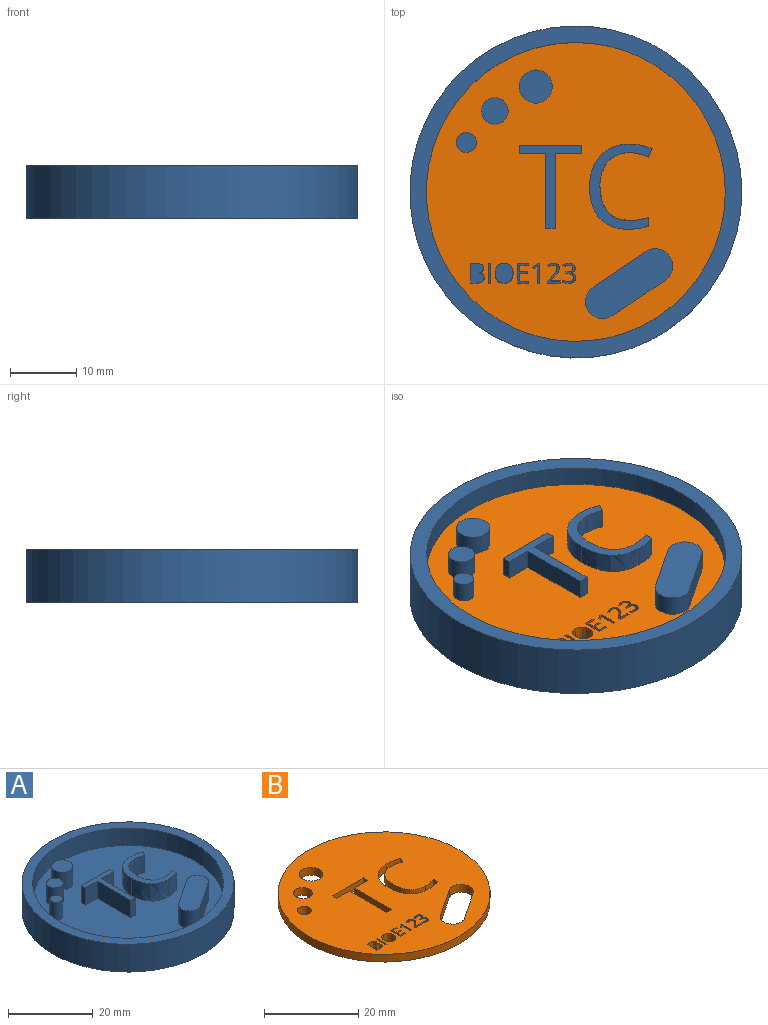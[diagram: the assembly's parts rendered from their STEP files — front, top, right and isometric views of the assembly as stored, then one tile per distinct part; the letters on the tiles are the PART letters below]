
ASSEMBLY  parts=2 mates=1
PART A: 41 faces, bbox 50x50x8 mm
  f0: cylinder r=22.5mm len=45mm, axis (0,0,-1), area 706.9mm2, adj f2,f40
  f1: cylinder r=25mm len=50mm, axis (0,0,-1), area 1256.6mm2, adj f2,f3
  f2: plane 50x50mm, normal (0,0,1), area 373.1mm2, adj f0,f1
  f3: plane 50x50mm, normal (0,0,-1), area 1963.5mm2, adj f1
  f4: cylinder r=1.5mm len=5mm, axis (0,0,-1), area 47.1mm2, adj f5,f40
  f5: plane 3x3mm, normal (0,0,1), area 7.1mm2, adj f4
  f6: cylinder r=2mm len=5mm, axis (0,0,-1), area 62.8mm2, adj f7,f40
  f7: plane 4x4mm, normal (0,0,1), area 12.6mm2, adj f6
  f8: cylinder r=2.5mm len=5mm, axis (0,0,-1), area 78.5mm2, adj f9,f40
  f9: plane 5x5mm, normal (0,0,1), area 19.6mm2, adj f8
  f10: plane 11.18x5mm, normal (1,0,0), area 55.9mm2, adj f11,f17,f18,f40
  f11: plane 5x3.95mm, normal (0,-1,0), area 19.7mm2, adj f10,f12,f18,f40
  f12: plane 5x1.29mm, normal (1,0,0), area 6.4mm2, adj f11,f13,f18,f40
  f13: plane 9.34x5mm, normal (0,1,0), area 46.7mm2, adj f12,f14,f18,f40
  f14: plane 5x1.29mm, normal (-1,0,0), area 6.4mm2, adj f13,f15,f18,f40
  f15: plane 5x3.95mm, normal (0,-1,0), area 19.7mm2, adj f14,f16,f18,f40
  f16: plane 11.18x5mm, normal (-1,0,0), area 55.9mm2, adj f15,f17,f18,f40
  f17: plane 5x1.45mm, normal (0,-1,0), area 7.2mm2, adj f10,f16,f18,f40
  f18: plane 12.47x9.34mm, normal (0,0,1), area 28.2mm2, adj f10,f11,f12,f13,f14,f15,f16,f17
  f19: extruded ~5x2.83mm, area 14.7mm2, adj f20,f33,f34,f40
  f20: plane 5x1.24mm, normal (0.9,-0.44,0), area 6.9mm2, adj f19,f21,f34,f40
  f21: extruded ~5x3.43mm, area 17.7mm2, adj f20,f22,f34,f40
  f22: extruded ~5x3.2mm, area 16.7mm2, adj f21,f23,f34,f40
  f23: extruded ~5x2.23mm, area 15.5mm2, adj f22,f24,f34,f40
  f24: extruded ~5x3.37mm, area 17.4mm2, adj f23,f25,f34,f40
  f25: extruded ~5x4.75mm, area 25.5mm2, adj f24,f26,f34,f40
  f26: extruded ~5x4.25mm, area 23.6mm2, adj f25,f27,f34,f40
  f27: extruded ~5x3.2mm, area 16.3mm2, adj f26,f28,f34,f40
  f28: plane 5x1.27mm, normal (1,0,0), area 6.3mm2, adj f27,f29,f34,f40
  f29: extruded ~5x2.98mm, area 15.1mm2, adj f28,f30,f34,f40
  f30: extruded ~5x3.27mm, area 18.3mm2, adj f29,f31,f34,f40
  f31: extruded ~5x3.78mm, area 20.2mm2, adj f30,f32,f34,f40
  f32: extruded ~5x3.75mm, area 20.1mm2, adj f31,f33,f34,f40
  f33: extruded ~5x3.24mm, area 18.2mm2, adj f19,f32,f34,f40
  f34: plane 12.81x9.43mm, normal (0,0,1), area 34mm2, adj f19,f20,f21,f22,f23,f24,f25,f26
  f35: plane 7.94x5.33mm, normal (-0.56,0.83,0), area 47.8mm2, adj f36,f38,f39,f40
  f36: cylinder r=2.61mm len=5mm, axis (0,0,-1), area 41mm2, adj f35,f37,f39,f40
  f37: plane 7.94x5.33mm, normal (0.56,-0.83,0), area 47.8mm2, adj f36,f38,f39,f40
  f38: cylinder r=2.61mm len=5mm, axis (0,0,-1), area 41mm2, adj f35,f37,f39,f40
  f39: plane 13.15x10.55mm, normal (0,0,1), area 71.2mm2, adj f35,f36,f37,f38
  f40: plane 45x45mm, normal (0,0,1), area 1417.7mm2, adj f0,f4,f6,f8,f10,f11,f12,f13
PART B: 125 faces, bbox 45x45x2 mm
  f0: plane 7.94x5.33mm, normal (0.56,-0.83,0), area 19.1mm2, adj f1,f109,f123,f124
  f1: cylinder r=2.61mm len=4.77mm, axis (0,0,-1), area 16.4mm2, adj f0,f2,f123,f124
  f2: plane 7.94x5.33mm, normal (-0.56,0.83,0), area 19.1mm2, adj f1,f109,f123,f124
  f3: plane 3.95x2mm, normal (0,1,0), area 7.9mm2, adj f4,f110,f123,f124
  f4: plane 11.18x2mm, normal (-1,0,0), area 22.4mm2, adj f3,f5,f123,f124
  f5: plane 2x1.45mm, normal (0,1,0), area 2.9mm2, adj f4,f6,f123,f124
  f6: plane 11.18x2mm, normal (1,0,0), area 22.4mm2, adj f5,f7,f123,f124
  f7: plane 3.95x2mm, normal (0,1,0), area 7.9mm2, adj f6,f8,f123,f124
  f8: plane 2x1.29mm, normal (1,0,0), area 2.6mm2, adj f7,f9,f123,f124
  f9: plane 9.34x2mm, normal (0,-1,0), area 18.7mm2, adj f8,f110,f123,f124
  f10: plane 2x1.24mm, normal (-0.9,0.44,0), area 2.8mm2, adj f11,f111,f123,f124
  f11: extruded ~2.83x2mm, area 5.9mm2, adj f10,f12,f123,f124
  f12: extruded ~3.24x2mm, area 7.3mm2, adj f11,f13,f123,f124
  f13: extruded ~3.75x2mm, area 8mm2, adj f12,f14,f123,f124
  f14: extruded ~3.78x2mm, area 8.1mm2, adj f13,f15,f123,f124
  f15: extruded ~3.27x2mm, area 7.3mm2, adj f14,f16,f123,f124
  f16: extruded ~2.98x2mm, area 6mm2, adj f15,f17,f123,f124
  f17: plane 2x1.27mm, normal (-1,0,0), area 2.5mm2, adj f16,f18,f123,f124
  f18: extruded ~3.2x2mm, area 6.5mm2, adj f17,f19,f123,f124
  f19: extruded ~4.25x2mm, area 9.4mm2, adj f18,f20,f123,f124
  f20: extruded ~4.75x2mm, area 10.2mm2, adj f19,f21,f123,f124
  f21: extruded ~3.37x2mm, area 7mm2, adj f20,f22,f123,f124
  f22: extruded ~2.23x2.08mm, area 6.2mm2, adj f21,f23,f123,f124
  f23: extruded ~3.2x2mm, area 6.7mm2, adj f22,f111,f123,f124
  f24: plane 2x1.03mm, normal (0,1,0), area 2.1mm2, adj f25,f112,f123,f124
  f25: plane 2.96x2mm, normal (1,0,0), area 5.9mm2, adj f24,f26,f123,f124
  f26: plane 2x0.84mm, normal (0,-1,0), area 1.7mm2, adj f25,f27,f123,f124
  f27: extruded ~2x0.85mm, area 1.8mm2, adj f26,f28,f123,f124
  f28: extruded ~2x0.56mm, area 1.3mm2, adj f27,f29,f123,f124
  f29: extruded ~2x0.43mm, area 0.9mm2, adj f28,f30,f123,f124
  f30: extruded ~2x0.43mm, area 1mm2, adj f29,f31,f123,f124
  f31: plane 2x0.02mm, normal (-1,0,0), area 0mm2, adj f30,f32,f123,f124
  f32: extruded ~2x0.71mm, area 2.2mm2, adj f31,f33,f123,f124
  f33: extruded ~2x0.62mm, area 1.4mm2, adj f32,f112,f123,f124
  f34: plane 2.96x2mm, normal (-1,0,0), area 5.9mm2, adj f35,f113,f123,f124
  f35: plane 2x0.34mm, normal (0,1,0), area 0.7mm2, adj f34,f36,f123,f124
  f36: plane 2.96x2mm, normal (1,0,0), area 5.9mm2, adj f35,f113,f123,f124
  f37: extruded ~2x1mm, area 2.2mm2, adj f38,f114,f123,f124
  f38: extruded ~2x1.12mm, area 2.4mm2, adj f37,f39,f123,f124
  f39: extruded ~2x1.12mm, area 2.4mm2, adj f38,f40,f123,f124
  f40: extruded ~2x1mm, area 2.2mm2, adj f39,f41,f123,f124
  f41: extruded ~2x1.01mm, area 2.2mm2, adj f40,f42,f123,f124
  f42: extruded ~2x1.13mm, area 2.4mm2, adj f41,f43,f123,f124
  f43: extruded ~2x1.12mm, area 2.4mm2, adj f42,f114,f123,f124
  f44: plane 2x1.31mm, normal (0,-1,0), area 2.6mm2, adj f45,f115,f123,f124
  f45: plane 2x0.31mm, normal (-1,0,0), area 0.6mm2, adj f44,f46,f123,f124
  f46: plane 2x1.65mm, normal (0,1,0), area 3.3mm2, adj f45,f47,f123,f124
  f47: plane 2.96x2mm, normal (1,0,0), area 5.9mm2, adj f46,f48,f123,f124
  f48: plane 2x1.65mm, normal (0,-1,0), area 3.3mm2, adj f47,f49,f123,f124
  f49: plane 2x0.31mm, normal (-1,0,0), area 0.6mm2, adj f48,f50,f123,f124
  f50: plane 2x1.31mm, normal (0,1,0), area 2.6mm2, adj f49,f51,f123,f124
  f51: plane 2x0.95mm, normal (-1,0,0), area 1.9mm2, adj f50,f52,f123,f124
  f52: plane 2x1.23mm, normal (0,-1,0), area 2.5mm2, adj f51,f53,f123,f124
  f53: plane 2x0.3mm, normal (-1,0,0), area 0.6mm2, adj f52,f54,f123,f124
  f54: plane 2x1.23mm, normal (0,1,0), area 2.5mm2, adj f53,f115,f123,f124
  f55: plane 2x0.28mm, normal (0,-1,0), area 0.6mm2, adj f56,f116,f123,f124
  f56: plane 2.96x2mm, normal (-1,0,0), area 5.9mm2, adj f55,f57,f123,f124
  f57: plane 2x0.33mm, normal (0,1,0), area 0.7mm2, adj f56,f58,f123,f124
  f58: plane 2.11x2mm, normal (1,0,0), area 4.2mm2, adj f57,f59,f123,f124
  f59: extruded ~2x0.5mm, area 1mm2, adj f58,f60,f123,f124
  f60: extruded ~2x0.1mm, area 0.3mm2, adj f59,f61,f123,f124
  f61: extruded ~2x0.48mm, area 1.2mm2, adj f60,f62,f123,f124
  f62: plane 2x0.23mm, normal (0.79,0.61,0), area 0.6mm2, adj f61,f116,f123,f124
  f63: plane 2x1.52mm, normal (0,-1,0), area 3mm2, adj f64,f117,f123,f124
  f64: plane 2x0.31mm, normal (-1,0,0), area 0.6mm2, adj f63,f65,f123,f124
  f65: plane 2x1.95mm, normal (0,1,0), area 3.9mm2, adj f64,f66,f123,f124
  f66: plane 2x0.29mm, normal (1,0,0), area 0.6mm2, adj f65,f67,f123,f124
  f67: plane 2x0.78mm, normal (0.71,-0.71,0), area 2.2mm2, adj f66,f68,f123,f124
  f68: extruded ~2x0.51mm, area 1.4mm2, adj f67,f69,f123,f124
  f69: extruded ~2x0.3mm, area 0.7mm2, adj f68,f70,f123,f124
  f70: extruded ~2x0.31mm, area 0.6mm2, adj f69,f71,f123,f124
  f71: extruded ~2x0.38mm, area 0.8mm2, adj f70,f72,f123,f124
  f72: extruded ~2x0.4mm, area 0.9mm2, adj f71,f73,f123,f124
  f73: extruded ~2x0.35mm, area 0.7mm2, adj f72,f74,f123,f124
  f74: extruded ~2x0.37mm, area 0.9mm2, adj f73,f75,f123,f124
  f75: plane 2x0.23mm, normal (0.79,0.61,0), area 0.6mm2, adj f74,f76,f123,f124
  f76: extruded ~2x0.89mm, area 1.9mm2, adj f75,f77,f123,f124
  f77: extruded ~2x0.65mm, area 1.4mm2, adj f76,f78,f123,f124
  f78: extruded ~2x0.57mm, area 1.3mm2, adj f77,f79,f123,f124
  f79: extruded ~2x0.56mm, area 1.2mm2, adj f78,f80,f123,f124
  f80: extruded ~2x0.7mm, area 1.8mm2, adj f79,f81,f123,f124
  f81: plane 2x0.65mm, normal (-0.7,0.71,0), area 1.8mm2, adj f80,f117,f123,f124
  f82: extruded ~2x0.67mm, area 1.4mm2, adj f83,f118,f123,f124
  f83: extruded ~2x0.54mm, area 1.2mm2, adj f82,f84,f123,f124
  f84: extruded ~2x0.46mm, area 1mm2, adj f83,f85,f123,f124
  f85: extruded ~2x0.45mm, area 1mm2, adj f84,f86,f123,f124
  f86: plane 2x0.02mm, normal (-1,0,0), area 0mm2, adj f85,f87,f123,f124
  f87: extruded ~2x0.53mm, area 1.2mm2, adj f86,f88,f123,f124
  f88: extruded ~2x0.48mm, area 1mm2, adj f87,f89,f123,f124
  f89: extruded ~2x0.65mm, area 1.5mm2, adj f88,f90,f123,f124
  f90: extruded ~2x0.83mm, area 1.8mm2, adj f89,f91,f123,f124
  f91: extruded ~2x0.43mm, area 0.9mm2, adj f90,f92,f123,f124
  f92: extruded ~2x0.38mm, area 0.8mm2, adj f91,f93,f123,f124
  f93: plane 2x0.32mm, normal (1,0,0), area 0.6mm2, adj f92,f94,f123,f124
  f94: extruded ~2x0.41mm, area 0.9mm2, adj f93,f95,f123,f124
  f95: extruded ~2x0.41mm, area 0.8mm2, adj f94,f96,f123,f124
  f96: extruded ~2x0.77mm, area 2.2mm2, adj f95,f97,f123,f124
  f97: extruded ~2x0.85mm, area 2.3mm2, adj f96,f98,f123,f124
  f98: plane 2x0.29mm, normal (0,1,0), area 0.6mm2, adj f97,f99,f123,f124
  f99: plane 2x0.29mm, normal (1,0,0), area 0.6mm2, adj f98,f100,f123,f124
  f100: plane 2x0.3mm, normal (0,-1,0), area 0.6mm2, adj f99,f101,f123,f124
  f101: extruded ~2x0.55mm, area 1.2mm2, adj f100,f102,f123,f124
  f102: extruded ~2x0.42mm, area 1mm2, adj f101,f103,f123,f124
  f103: extruded ~2x0.34mm, area 0.8mm2, adj f102,f104,f123,f124
  f104: extruded ~2x0.4mm, area 0.9mm2, adj f103,f105,f123,f124
  f105: extruded ~2x0.37mm, area 0.7mm2, adj f104,f106,f123,f124
  f106: extruded ~2x0.39mm, area 0.9mm2, adj f105,f107,f123,f124
  f107: plane 2x0.23mm, normal (0.8,0.6,0), area 0.6mm2, adj f106,f108,f123,f124
  f108: extruded ~2x0.42mm, area 1mm2, adj f107,f118,f123,f124
  f109: cylinder r=2.61mm len=4.77mm, axis (0,0,-1), area 16.4mm2, adj f0,f2,f123,f124
  f110: plane 2x1.29mm, normal (-1,0,0), area 2.6mm2, adj f3,f9,f123,f124
  f111: extruded ~3.43x2mm, area 7.1mm2, adj f10,f23,f123,f124
  f112: extruded ~2x0.75mm, area 1.6mm2, adj f24,f33,f123,f124
  f113: plane 2x0.34mm, normal (0,-1,0), area 0.7mm2, adj f34,f36,f123,f124
  f114: extruded ~2x1.01mm, area 2.2mm2, adj f37,f43,f123,f124
  f115: plane 2x1.09mm, normal (-1,0,0), area 2.2mm2, adj f44,f54,f123,f124
  f116: plane 2x0.78mm, normal (0.61,-0.79,0), area 2mm2, adj f55,f62,f123,f124
  f117: plane 2x0.02mm, normal (-1,0,0), area 0mm2, adj f63,f81,f123,f124
  f118: extruded ~2x0.5mm, area 1mm2, adj f82,f108,f123,f124
  f119: cylinder r=1.5mm len=3mm, axis (0,0,-1), area 18.8mm2, adj f123,f124
  f120: cylinder r=2mm len=4mm, axis (0,0,-1), area 25.1mm2, adj f123,f124
  f121: cylinder r=2.5mm len=5mm, axis (0,0,-1), area 31.4mm2, adj f123,f124
  f122: cylinder r=22.5mm len=45mm, axis (0,0,-1), area 282.7mm2, adj f123,f124
  f123: plane 45x45mm, normal (0,0,1), area 1397.1mm2, adj f0,f1,f2,f3,f4,f5,f6,f7
  f124: plane 45x45mm, normal (0,0,-1), area 1397.1mm2, adj f0,f1,f2,f3,f4,f5,f6,f7
PLACE A t=(0.15,-0.34,3.28)mm
PLACE B t=(0.15,-0.34,3.28)mm
MATE fastened A.f0 <-> B.f122  axis (0,0,1) through (0.15,-0.34,3.28)mm
